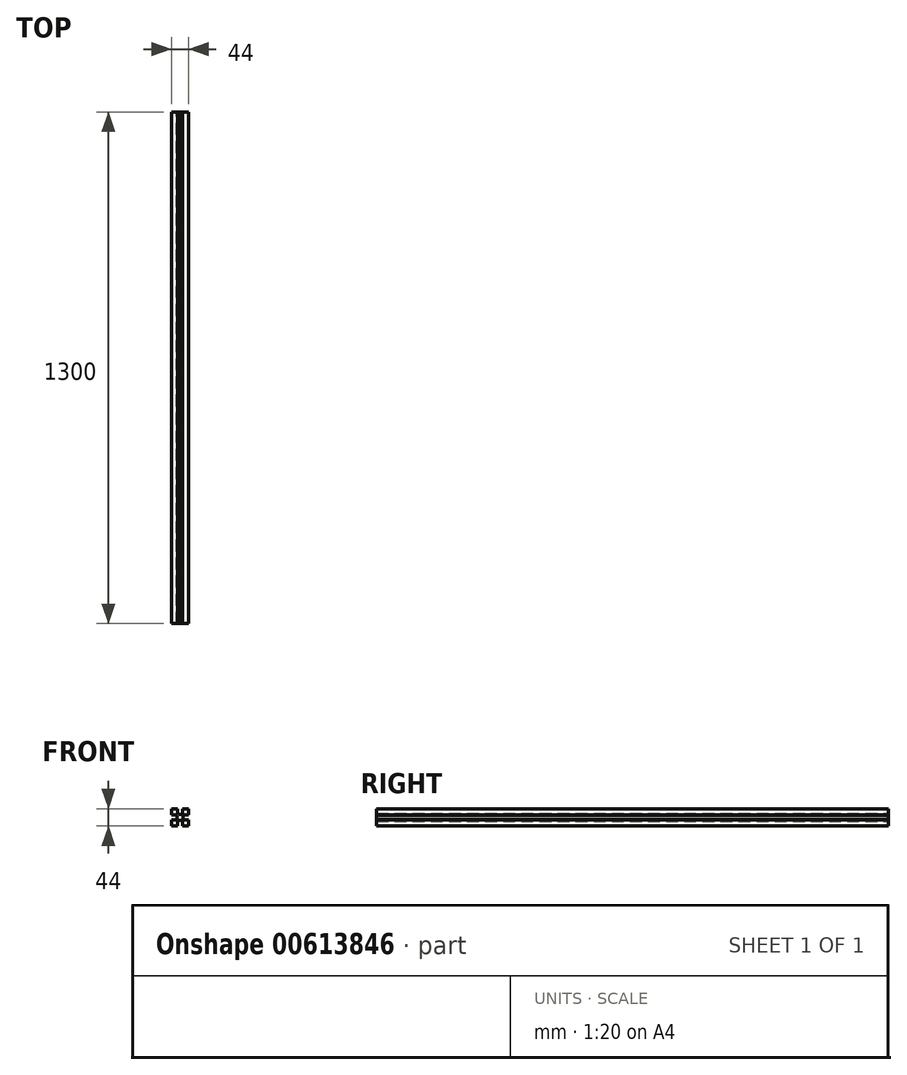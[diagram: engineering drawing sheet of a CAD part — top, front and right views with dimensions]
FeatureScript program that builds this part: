
annotation { "Feature Type Name" : "Feature", "Feature Type Description" : "" }
export const myFeature = defineFeature(function(context is Context, id is Id, definition is map)
    precondition{}
    {
        {
            var Q0;
            Q0=qCreatedBy(makeId("Front.planeOp"),FACE);
            var sketch = newSketch(context, id + "F0", { "sketchPlane" : qUnion([Q0])});
            skPoint(sketch, "E0.middle", {"position": v(0, 0) * mm});
            skLineSegment(sketch, "E1.bottom", {"start": v(22, -22) * mm, "end": v(6, -22) * mm});
            skLineSegment(sketch, "E1.left", {"start": v(22, -22) * mm, "end": v(22, -6) * mm});
            skCircle(sketch, "E2", {"center": v(0, 0) * mm, "radius": 8 * mm});
            skPoint(sketch, "E3", {"position": v(22, 0) * mm});
            skPoint(sketch, "E3.positionSnap0", {"position": v(22, -14) * mm});
            skPoint(sketch, "E4", {"position": v(0, -22) * mm});
            skLineSegment(sketch, "E5", {"start": v(6, -22) * mm, "end": v(6, -10.43) * mm});
            skLineSegment(sketch, "E6", {"start": v(6, -10.43) * mm, "end": v(3.66, -7.11) * mm});
            skLineSegment(sketch, "E7", {"start": v(22, -6) * mm, "end": v(9.13, -6) * mm});
            skLineSegment(sketch, "E8", {"start": v(9.13, -6) * mm, "end": v(6.01, -5.28) * mm});
            skLineSegment(sketch, "E9.MirrorCS", {"start": v(-6, -22) * mm, "end": v(-6, -10.43) * mm});
            skLineSegment(sketch, "E10.MirrorCS", {"start": v(-22, -22) * mm, "end": v(-6, -22) * mm});
            skLineSegment(sketch, "E11.MirrorCS", {"start": v(-22, -22) * mm, "end": v(-22, -6) * mm});
            skLineSegment(sketch, "E12.MirrorCS", {"start": v(-22, -6) * mm, "end": v(-9.13, -6) * mm});
            skLineSegment(sketch, "E13.MirrorCS", {"start": v(-6, -10.43) * mm, "end": v(-3.66, -7.11) * mm});
            skLineSegment(sketch, "E14.MirrorCS", {"start": v(-9.13, -6) * mm, "end": v(-6.01, -5.28) * mm});
            skLineSegment(sketch, "E15.MirrorCS", {"start": v(22, 22) * mm, "end": v(22, 6) * mm});
            skLineSegment(sketch, "E16.MirrorCS", {"start": v(22, 6) * mm, "end": v(9.13, 6) * mm});
            skLineSegment(sketch, "E17.MirrorCS", {"start": v(22, 22) * mm, "end": v(6, 22) * mm});
            skLineSegment(sketch, "E18.MirrorCS", {"start": v(6, 22) * mm, "end": v(6, 10.43) * mm});
            skLineSegment(sketch, "E19.MirrorCS", {"start": v(6, 10.43) * mm, "end": v(3.66, 7.11) * mm});
            skLineSegment(sketch, "E20.MirrorCS", {"start": v(9.13, 6) * mm, "end": v(6.01, 5.28) * mm});
            skLineSegment(sketch, "E21.MirrorCS", {"start": v(-6, 10.43) * mm, "end": v(-3.66, 7.11) * mm});
            skLineSegment(sketch, "E22.MirrorCS", {"start": v(-9.13, 6) * mm, "end": v(-6.01, 5.28) * mm});
            skLineSegment(sketch, "E23.MirrorCS", {"start": v(-6, 22) * mm, "end": v(-6, 10.43) * mm});
            skLineSegment(sketch, "E24.MirrorCS", {"start": v(-22, 22) * mm, "end": v(-6, 22) * mm});
            skLineSegment(sketch, "E25.MirrorCS", {"start": v(-22, 22) * mm, "end": v(-22, 6) * mm});
            skLineSegment(sketch, "E26.MirrorCS", {"start": v(-22, 6) * mm, "end": v(-9.13, 6) * mm});
            skSolve(sketch);
        }
        {
            var Q0;
            Q0 = qSketchRegion(id + "F0", true);
            extrude(context, id + "F1", {"entities" : qUnion([Q0]), "endBound" : BoundingType.SYMMETRIC, "depth" : 1300 * mm, "offsetDistance" : 25.4 * mm});
        }
    });
